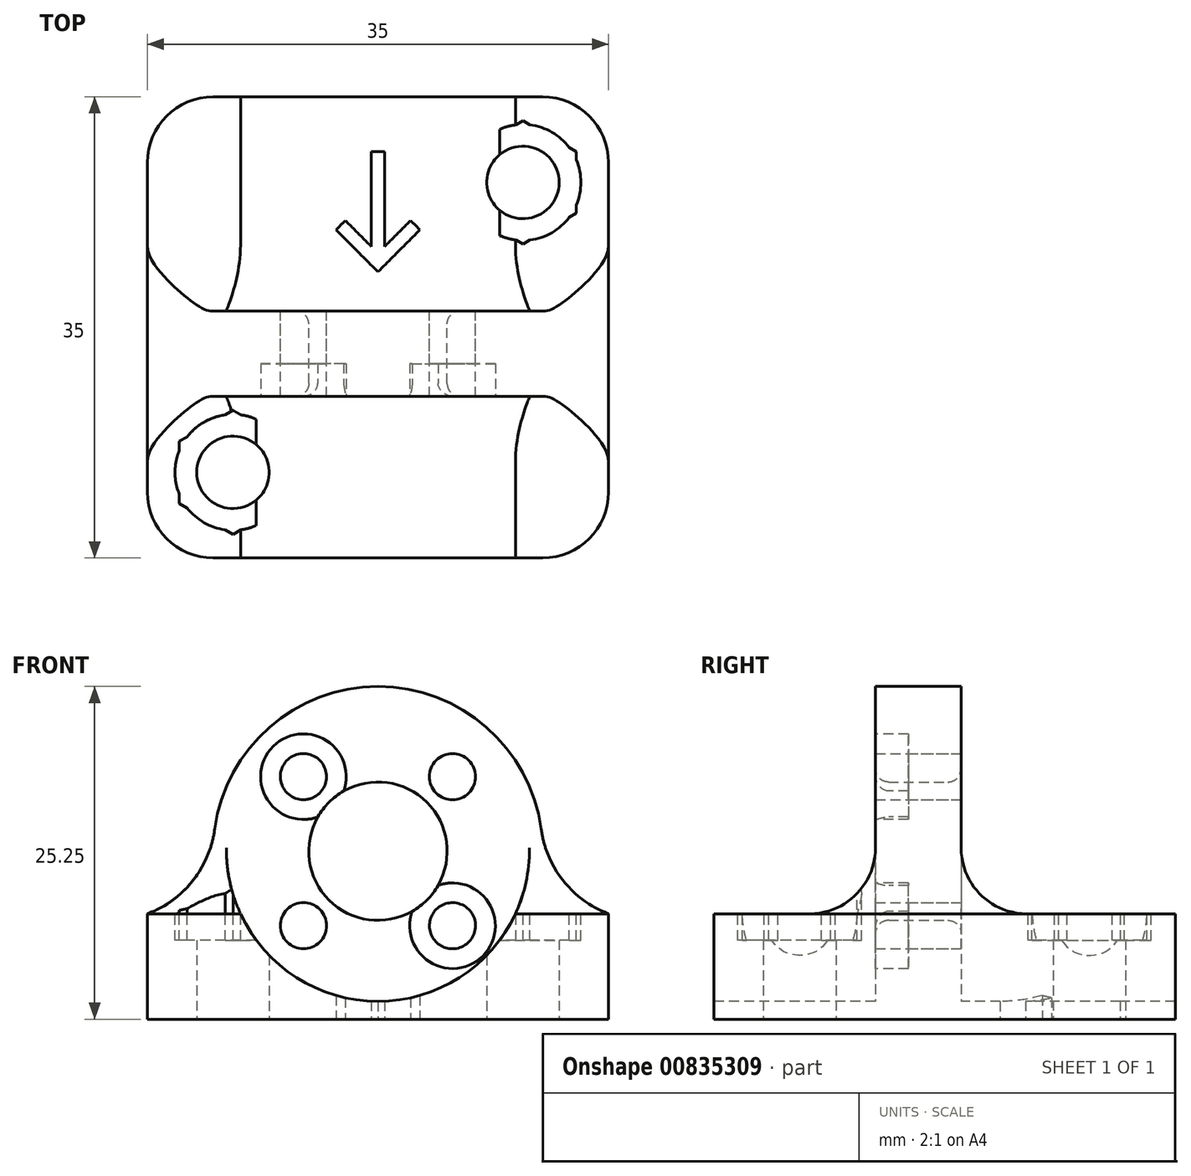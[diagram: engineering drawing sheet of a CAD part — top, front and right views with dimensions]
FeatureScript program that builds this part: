
annotation { "Feature Type Name" : "Feature", "Feature Type Description" : "" }
export const myFeature = defineFeature(function(context is Context, id is Id, definition is map)
    precondition{}
    {
        {
            var Q0;
            Q0=qCreatedBy(makeId("Front.planeOp"),FACE);
            cPlane(context, id + "F0", {"entities" : qUnion([Q0]), "cplaneType" : CPlaneType.OFFSET, "offset" : 2 * mm, "width" : 150 * mm, "height" : 150 * mm});
        }
        {
            var Q0;
            Q0=qCreatedBy(makeId("Top.planeOp"),FACE);
            var sketch = newSketch(context, id + "F1", { "sketchPlane" : qUnion([Q0])});
            skLineSegment(sketch, "E0.bottom", {"start": v(-17.5, 17.5) * mm, "end": v(17.5, 17.5) * mm});
            skLineSegment(sketch, "E0.top", {"start": v(-17.5, -17.5) * mm, "end": v(17.5, -17.5) * mm});
            skLineSegment(sketch, "E0.left", {"start": v(-17.5, 17.5) * mm, "end": v(-17.5, -17.5) * mm});
            skLineSegment(sketch, "E0.right", {"start": v(17.5, 17.5) * mm, "end": v(17.5, -17.5) * mm});
            skPoint(sketch, "E0.middle", {"position": v(0, 0) * mm});
            skLineSegment(sketch, "E1.bottom", {"start": v(-11, 11) * mm, "end": v(11, 11) * mm, "construction": true});
            skLineSegment(sketch, "E1.top", {"start": v(-11, -11) * mm, "end": v(11, -11) * mm, "construction": true});
            skLineSegment(sketch, "E1.left", {"start": v(-11, 11) * mm, "end": v(-11, -11) * mm, "construction": true});
            skLineSegment(sketch, "E1.right", {"start": v(11, 11) * mm, "end": v(11, -11) * mm, "construction": true});
            skCircle(sketch, "E2", {"center": v(-11, 11) * mm, "radius": 2.75 * mm, "construction": true});
            skCircle(sketch, "E3", {"center": v(11, 11) * mm, "radius": 2.75 * mm});
            skCircle(sketch, "E4", {"center": v(11, -11) * mm, "radius": 2.75 * mm, "construction": true});
            skCircle(sketch, "E5", {"center": v(-11, -11) * mm, "radius": 2.75 * mm});
            skSolve(sketch);
        }
        {
            var Q0;
            Q0=qSketchRegion(id+"F1",true);
            extrude(context, id + "F2", {"entities" : qUnion([Q0]), "depth" : 8 * mm, "offsetDistance" : 25 * mm});
        }
        {
            var Q0;
            Q0=qCreatedBy(id+"F0.planeOp",FACE);
            var sketch = newSketch(context, id + "F3", { "sketchPlane" : qUnion([Q0])});
            skLineSegment(sketch, "E6", {"start": v(0, 0) * mm, "end": v(0, 12.75) * mm, "construction": true});
            skArc(sketch, "E7", {"start": v(12.5, 12.75) * mm, "mid": v(0, 25.25) * mm, "end": v(-12.5, 12.75) * mm});
            skLineSegment(sketch, "E8", {"start": v(-12.5, 12.75) * mm, "end": v(-12.5, 0) * mm});
            skLineSegment(sketch, "E9.MirrorCS", {"start": v(12.5, 12.75) * mm, "end": v(12.5, 0) * mm});
            skCircle(sketch, "E10", {"center": v(0, 12.75) * mm, "radius": 5.25 * mm});
            skCircle(sketch, "E11", {"center": v(0, 12.75) * mm, "radius": 8 * mm, "construction": true});
            skLineSegment(sketch, "E12", {"start": v(0, 20.75) * mm, "end": v(0, 4.75) * mm, "construction": true});
            skPoint(sketch, "E12.startSnap0", {"position": v(0, 25.25) * mm});
            skLineSegment(sketch, "E13", {"start": v(-8, 12.75) * mm, "end": v(8, 12.75) * mm, "construction": true});
            skLineSegment(sketch, "E14", {"start": v(0, 12.75) * mm, "end": v(-5.66, 18.4) * mm, "construction": true});
            skLineSegment(sketch, "E15", {"start": v(0, 12.75) * mm, "end": v(-5.66, 7.1) * mm, "construction": true});
            skLineSegment(sketch, "E16.MirrorCS", {"start": v(0, 12.75) * mm, "end": v(5.66, 18.4) * mm, "construction": true});
            skLineSegment(sketch, "E17.MirrorCS", {"start": v(0, 12.75) * mm, "end": v(5.66, 7.1) * mm, "construction": true});
            skCircle(sketch, "E18", {"center": v(-5.66, 18.4) * mm, "radius": 1.75 * mm});
            skCircle(sketch, "E19", {"center": v(-5.66, 7.1) * mm, "radius": 1.75 * mm});
            skCircle(sketch, "E20", {"center": v(5.66, 7.1) * mm, "radius": 1.75 * mm});
            skCircle(sketch, "E21", {"center": v(5.66, 18.4) * mm, "radius": 1.75 * mm});
            skLineSegment(sketch, "E22", {"start": v(-12.5, 0) * mm, "end": v(12.5, 0) * mm});
            skSolve(sketch);
        }
        {
            var Q0;
            Q0=qCreatedBy(makeId("Front.planeOp"),FACE);
            var sketch = newSketch(context, id + "F4", { "sketchPlane" : qUnion([Q0])});
            skLineSegment(sketch, "E23", {"start": v(0, 0) * mm, "end": v(0, 12.85) * mm, "construction": true});
            skCircle(sketch, "E24", {"center": v(0, 12.85) * mm, "radius": 11.5 * mm});
            skSolve(sketch);
        }
        {
            var Q0;
            Q0=qSketchRegion(id+"F4",true);
            extrude(context, id + "F5", {"entities" : qUnion([Q0]), "operationType" : NewBodyOperationType.REMOVE, "endBound" : BoundingType.SYMMETRIC, "oppositeDirection" : true, "depth" : 36 * mm, "offsetDistance" : 25 * mm});
        }
        {
            var Q0;
            Q0=qSketchRegion(id+"F3",true);
            extrude(context, id + "F6", {"entities" : qUnion([Q0]), "operationType" : NewBodyOperationType.ADD, "endBound" : BoundingType.SYMMETRIC, "depth" : 6.5 * mm, "offsetDistance" : 25 * mm});
        }
        {
            var Q0;
            {var subQ0=sQuery(id+"F1.wireOp",EDGE,"E4");var subQ1=sQuery(id+"F1.wireOp",EDGE,"E0.top");var subQ2=sQuery(id+"F1.wireOp",EDGE,"E0.right");var subQ3=sQuery(id+"F1.wireOp",EDGE,"E0.bottom");Q0=makeQuery(id+"F6.boolean.opBoolean","INTERSECT",EDGE,{"derivedFrom":[makeQuery(id+"F5.boolean.opBoolean","SPLIT",FACE,{"disambiguationData":[TD([makeQuery(id+"F2.opExtrude","SWEPT_FACE",FACE,{"disambiguationData":[OSD([subQ2])]})])],"derivedFrom":makeQuery(id+"F2.opExtrude","CAP_FACE",FACE,{"disambiguationData":[OSD([subQ3,subQ1,sQuery(id+"F1.wireOp",EDGE,"E0.left"),subQ2,sQuery(id+"F1.wireOp",EDGE,"E2"),subQ0])],"isStart":false})}),makeQuery(id+"F6.opExtrude","SWEPT_FACE",FACE,{"disambiguationData":[OSD([sQuery(id+"F3.wireOp",EDGE,"E9.MirrorCS")])]})]});}
            var Q1;
            {var subQ0=sQuery(id+"F1.wireOp",EDGE,"E2");var subQ1=sQuery(id+"F1.wireOp",EDGE,"E0.left");var subQ2=sQuery(id+"F1.wireOp",EDGE,"E0.top");var subQ3=sQuery(id+"F1.wireOp",EDGE,"E0.bottom");Q1=makeQuery(id+"F6.boolean.opBoolean","INTERSECT",EDGE,{"derivedFrom":[makeQuery(id+"F5.boolean.opBoolean","SPLIT",FACE,{"disambiguationData":[TD([makeQuery(id+"F2.opExtrude","SWEPT_FACE",FACE,{"disambiguationData":[OSD([subQ1])]})])],"derivedFrom":makeQuery(id+"F2.opExtrude","CAP_FACE",FACE,{"disambiguationData":[OSD([subQ3,subQ2,subQ1,sQuery(id+"F1.wireOp",EDGE,"E0.right"),subQ0,sQuery(id+"F1.wireOp",EDGE,"E4")])],"isStart":false})}),makeQuery(id+"F6.opExtrude","SWEPT_FACE",FACE,{"disambiguationData":[OSD([sQuery(id+"F3.wireOp",EDGE,"E8")])]})]});}
            fillet(context, id + "F7", {"entities" : qUnion([Q0, Q1]), "radius" : 8 * mm, "tangentPropagation" : true, "allowEdgeOverflow" : false});
        }
        {
            var Q0;
            {var subQ0=sQuery(id+"F1.wireOp",EDGE,"E2");var subQ1=sQuery(id+"F1.wireOp",EDGE,"E0.left");var subQ2=sQuery(id+"F1.wireOp",EDGE,"E0.top");var subQ3=sQuery(id+"F1.wireOp",EDGE,"E0.bottom");Q0=makeQuery(id+"F7.opFillet","SPLIT",FACE,{"disambiguationData":[OD(0.0)],"derivedFrom":makeQuery(id+"F5.boolean.opBoolean","SPLIT",FACE,{"disambiguationData":[TD([makeQuery(id+"F2.opExtrude","SWEPT_FACE",FACE,{"disambiguationData":[OSD([subQ1])]})])],"derivedFrom":makeQuery(id+"F2.opExtrude","CAP_FACE",FACE,{"disambiguationData":[OSD([subQ3,subQ2,subQ1,sQuery(id+"F1.wireOp",EDGE,"E0.right"),subQ0,sQuery(id+"F1.wireOp",EDGE,"E4")])],"isStart":false})})});}
            var sketch = newSketch(context, id + "F8", { "sketchPlane" : qUnion([Q0])});
            skPoint(sketch, "E25.0.midPoint.positionSnap0", {"position": v(5.2, -11) * mm});
            skLineSegment(sketch, "E26", {"start": v(17.5, 17.5) * mm, "end": v(-17.5, -17.5) * mm, "construction": true});
            skCircle(sketch, "E27.cCircle", {"center": v(11, 11) * mm, "radius": 4.05 * mm, "construction": true});
            skLineSegment(sketch, "E27.0", {"start": v(15.05, 13.34) * mm, "end": v(15.05, 8.66) * mm});
            skLineSegment(sketch, "E27.1", {"start": v(15.05, 8.66) * mm, "end": v(11, 6.32) * mm});
            skLineSegment(sketch, "E27.2", {"start": v(11, 6.32) * mm, "end": v(6.95, 8.66) * mm});
            skLineSegment(sketch, "E27.3", {"start": v(6.95, 8.66) * mm, "end": v(6.95, 13.34) * mm});
            skLineSegment(sketch, "E27.4", {"start": v(6.95, 13.34) * mm, "end": v(11, 15.68) * mm});
            skLineSegment(sketch, "E27.5", {"start": v(11, 15.68) * mm, "end": v(15.05, 13.34) * mm});
            skPoint(sketch, "E27.0.midPoint", {"position": v(15.05, 11) * mm});
            skCircle(sketch, "E28.cCircle", {"center": v(-11, -11) * mm, "radius": 4.08 * mm, "construction": true});
            skLineSegment(sketch, "E28.0", {"start": v(-11, -6.3) * mm, "end": v(-6.93, -8.65) * mm});
            skLineSegment(sketch, "E28.1", {"start": v(-6.93, -8.65) * mm, "end": v(-6.93, -13.35) * mm});
            skLineSegment(sketch, "E28.2", {"start": v(-6.93, -13.35) * mm, "end": v(-11, -15.7) * mm});
            skLineSegment(sketch, "E28.3", {"start": v(-11, -15.7) * mm, "end": v(-15.08, -13.35) * mm});
            skLineSegment(sketch, "E28.4", {"start": v(-15.07, -13.35) * mm, "end": v(-15.07, -8.65) * mm});
            skLineSegment(sketch, "E28.5", {"start": v(-15.07, -8.65) * mm, "end": v(-11, -6.3) * mm});
            skPoint(sketch, "E28.0.midPoint", {"position": v(-8.96, -7.47) * mm});
            skSolve(sketch);
        }
        {
            var Q0;
            Q0=qSketchRegion(id+"F8",true);
            extrude(context, id + "F9", {"entities" : qUnion([Q0]), "operationType" : NewBodyOperationType.REMOVE, "oppositeDirection" : true, "depth" : 2 * mm, "offsetDistance" : 25 * mm});
        }
        {
            var Q0;
            {var subQ0=sQuery(id+"F1.wireOp",EDGE,"E2");var subQ1=sQuery(id+"F1.wireOp",EDGE,"E0.left");var subQ2=sQuery(id+"F1.wireOp",EDGE,"E0.top");var subQ3=sQuery(id+"F1.wireOp",EDGE,"E0.bottom");Q0=makeQuery(id+"F7.opFillet","SPLIT",FACE,{"disambiguationData":[OD(0.0)],"derivedFrom":makeQuery(id+"F5.boolean.opBoolean","SPLIT",FACE,{"disambiguationData":[TD([makeQuery(id+"F2.opExtrude","SWEPT_FACE",FACE,{"disambiguationData":[OSD([subQ1])]})])],"derivedFrom":makeQuery(id+"F2.opExtrude","CAP_FACE",FACE,{"disambiguationData":[OSD([subQ3,subQ2,subQ1,sQuery(id+"F1.wireOp",EDGE,"E0.right"),subQ0,sQuery(id+"F1.wireOp",EDGE,"E4")])],"isStart":false})})});}
            var sketch = newSketch(context, id + "F10", { "sketchPlane" : qUnion([Q0])});
            skCircle(sketch, "E29", {"center": v(11, 11) * mm, "radius": 4.4 * mm});
            skCircle(sketch, "E30", {"center": v(-11, -11) * mm, "radius": 4.4 * mm});
            skSolve(sketch);
        }
        {
            var Q0;
            Q0=qSketchRegion(id+"F10",true);
            extrude(context, id + "F11", {"entities" : qUnion([Q0]), "operationType" : NewBodyOperationType.REMOVE, "oppositeDirection" : true, "depth" : 2 * mm, "offsetDistance" : 25 * mm});
        }
        {
            var Q0;
            {var subQ0=sQuery(id+"F1.wireOp",EDGE,"E4");var subQ1=sQuery(id+"F1.wireOp",EDGE,"E0.top");var subQ2=sQuery(id+"F1.wireOp",EDGE,"E0.right");var subQ3=sQuery(id+"F1.wireOp",EDGE,"E0.bottom");Q0=makeQuery(id+"F6.boolean.opBoolean","INTERSECT",EDGE,{"derivedFrom":[makeQuery(id+"F5.boolean.opBoolean","SPLIT",FACE,{"disambiguationData":[TD([makeQuery(id+"F2.opExtrude","SWEPT_FACE",FACE,{"disambiguationData":[OSD([subQ2])]})])],"derivedFrom":makeQuery(id+"F2.opExtrude","CAP_FACE",FACE,{"disambiguationData":[OSD([subQ3,subQ1,sQuery(id+"F1.wireOp",EDGE,"E0.left"),subQ2,sQuery(id+"F1.wireOp",EDGE,"E2"),subQ0])],"isStart":false})}),makeQuery(id+"F6.opExtrude","CAP_FACE",FACE,{"disambiguationData":[OSD([sQuery(id+"F3.wireOp",EDGE,"E7"),sQuery(id+"F3.wireOp",EDGE,"E8"),sQuery(id+"F3.wireOp",EDGE,"E9.MirrorCS"),sQuery(id+"F3.wireOp",EDGE,"E10"),sQuery(id+"F3.wireOp",EDGE,"E18"),sQuery(id+"F3.wireOp",EDGE,"E19"),sQuery(id+"F3.wireOp",EDGE,"E20"),sQuery(id+"F3.wireOp",EDGE,"E21"),sQuery(id+"F3.wireOp",EDGE,"E22")])],"isStart":true})]});}
            var Q1;
            {var subQ0=sQuery(id+"F1.wireOp",EDGE,"E2");var subQ1=sQuery(id+"F1.wireOp",EDGE,"E0.left");var subQ2=sQuery(id+"F1.wireOp",EDGE,"E0.top");var subQ3=sQuery(id+"F1.wireOp",EDGE,"E0.bottom");Q1=makeQuery(id+"F6.boolean.opBoolean","INTERSECT",EDGE,{"derivedFrom":[makeQuery(id+"F5.boolean.opBoolean","SPLIT",FACE,{"disambiguationData":[TD([makeQuery(id+"F2.opExtrude","SWEPT_FACE",FACE,{"disambiguationData":[OSD([subQ1])]})])],"derivedFrom":makeQuery(id+"F2.opExtrude","CAP_FACE",FACE,{"disambiguationData":[OSD([subQ3,subQ2,subQ1,sQuery(id+"F1.wireOp",EDGE,"E0.right"),subQ0,sQuery(id+"F1.wireOp",EDGE,"E4")])],"isStart":false})}),makeQuery(id+"F6.opExtrude","CAP_FACE",FACE,{"disambiguationData":[OSD([sQuery(id+"F3.wireOp",EDGE,"E7"),sQuery(id+"F3.wireOp",EDGE,"E8"),sQuery(id+"F3.wireOp",EDGE,"E9.MirrorCS"),sQuery(id+"F3.wireOp",EDGE,"E10"),sQuery(id+"F3.wireOp",EDGE,"E18"),sQuery(id+"F3.wireOp",EDGE,"E19"),sQuery(id+"F3.wireOp",EDGE,"E20"),sQuery(id+"F3.wireOp",EDGE,"E21"),sQuery(id+"F3.wireOp",EDGE,"E22")])],"isStart":true})]});}
            var Q2;
            {var subQ0=sQuery(id+"F1.wireOp",EDGE,"E2");var subQ1=sQuery(id+"F1.wireOp",EDGE,"E0.left");var subQ2=sQuery(id+"F1.wireOp",EDGE,"E0.top");var subQ3=sQuery(id+"F1.wireOp",EDGE,"E0.bottom");Q2=makeQuery(id+"F6.boolean.opBoolean","INTERSECT",EDGE,{"derivedFrom":[makeQuery(id+"F5.boolean.opBoolean","SPLIT",FACE,{"disambiguationData":[TD([makeQuery(id+"F2.opExtrude","SWEPT_FACE",FACE,{"disambiguationData":[OSD([subQ1])]})])],"derivedFrom":makeQuery(id+"F2.opExtrude","CAP_FACE",FACE,{"disambiguationData":[OSD([subQ3,subQ2,subQ1,sQuery(id+"F1.wireOp",EDGE,"E0.right"),subQ0,sQuery(id+"F1.wireOp",EDGE,"E4")])],"isStart":false})}),makeQuery(id+"F6.opExtrude","CAP_FACE",FACE,{"disambiguationData":[OSD([sQuery(id+"F3.wireOp",EDGE,"E7"),sQuery(id+"F3.wireOp",EDGE,"E8"),sQuery(id+"F3.wireOp",EDGE,"E9.MirrorCS"),sQuery(id+"F3.wireOp",EDGE,"E10"),sQuery(id+"F3.wireOp",EDGE,"E18"),sQuery(id+"F3.wireOp",EDGE,"E19"),sQuery(id+"F3.wireOp",EDGE,"E20"),sQuery(id+"F3.wireOp",EDGE,"E21"),sQuery(id+"F3.wireOp",EDGE,"E22")])],"isStart":false})]});}
            var Q3;
            {var subQ0=sQuery(id+"F1.wireOp",EDGE,"E4");var subQ1=sQuery(id+"F1.wireOp",EDGE,"E0.top");var subQ2=sQuery(id+"F1.wireOp",EDGE,"E0.right");var subQ3=sQuery(id+"F1.wireOp",EDGE,"E0.bottom");Q3=makeQuery(id+"F6.boolean.opBoolean","INTERSECT",EDGE,{"derivedFrom":[makeQuery(id+"F5.boolean.opBoolean","SPLIT",FACE,{"disambiguationData":[TD([makeQuery(id+"F2.opExtrude","SWEPT_FACE",FACE,{"disambiguationData":[OSD([subQ2])]})])],"derivedFrom":makeQuery(id+"F2.opExtrude","CAP_FACE",FACE,{"disambiguationData":[OSD([subQ3,subQ1,sQuery(id+"F1.wireOp",EDGE,"E0.left"),subQ2,sQuery(id+"F1.wireOp",EDGE,"E2"),subQ0])],"isStart":false})}),makeQuery(id+"F6.opExtrude","CAP_FACE",FACE,{"disambiguationData":[OSD([sQuery(id+"F3.wireOp",EDGE,"E7"),sQuery(id+"F3.wireOp",EDGE,"E8"),sQuery(id+"F3.wireOp",EDGE,"E9.MirrorCS"),sQuery(id+"F3.wireOp",EDGE,"E10"),sQuery(id+"F3.wireOp",EDGE,"E18"),sQuery(id+"F3.wireOp",EDGE,"E19"),sQuery(id+"F3.wireOp",EDGE,"E20"),sQuery(id+"F3.wireOp",EDGE,"E21"),sQuery(id+"F3.wireOp",EDGE,"E22")])],"isStart":false})]});}
            var Q4;
            Q4=makeQuery(id+"F2.opExtrude","SWEPT_EDGE",EDGE,{"disambiguationData":[OSD([sQuery(id+"F1.wireOp",EDGE,"E0.top"),sQuery(id+"F1.wireOp",EDGE,"E0.left")])]});
            var Q5;
            Q5=makeQuery(id+"F2.opExtrude","SWEPT_EDGE",EDGE,{"disambiguationData":[OSD([sQuery(id+"F1.wireOp",EDGE,"E0.bottom"),sQuery(id+"F1.wireOp",EDGE,"E0.left")])]});
            var Q6;
            Q6=makeQuery(id+"F2.opExtrude","SWEPT_EDGE",EDGE,{"disambiguationData":[OSD([sQuery(id+"F1.wireOp",EDGE,"E0.bottom"),sQuery(id+"F1.wireOp",EDGE,"E0.right")])]});
            var Q7;
            Q7=makeQuery(id+"F2.opExtrude","SWEPT_EDGE",EDGE,{"disambiguationData":[OSD([sQuery(id+"F1.wireOp",EDGE,"E0.top"),sQuery(id+"F1.wireOp",EDGE,"E0.right")])]});
            fillet(context, id + "F12", {"entities" : qUnion([Q0, Q1, Q2, Q3, Q4, Q5, Q6, Q7]), "radius" : 5 * mm, "tangentPropagation" : true, "allowEdgeOverflow" : false});
        }
        {
            var Q0;
            Q0=makeQuery(id+"F6.opExtrude","CAP_FACE",FACE,{"disambiguationData":[OSD([sQuery(id+"F3.wireOp",EDGE,"E7"),sQuery(id+"F3.wireOp",EDGE,"E8"),sQuery(id+"F3.wireOp",EDGE,"E9.MirrorCS"),sQuery(id+"F3.wireOp",EDGE,"E10"),sQuery(id+"F3.wireOp",EDGE,"E18"),sQuery(id+"F3.wireOp",EDGE,"E20"),sQuery(id+"F3.wireOp",EDGE,"E22")])],"isStart":false});
            var sketch = newSketch(context, id + "F13", { "sketchPlane" : qUnion([Q0])});
            skCircle(sketch, "E31", {"center": v(-5.66, 18.4) * mm, "radius": 3.25 * mm});
            skCircle(sketch, "E32", {"center": v(5.66, 7.1) * mm, "radius": 3.25 * mm});
            skLineSegment(sketch, "E33", {"start": v(0, 12.75) * mm, "end": v(12.71, 12.75) * mm, "construction": true});
            skCircle(sketch, "E34.MirrorC", {"center": v(5.66, 18.4) * mm, "radius": 3.25 * mm});
            skCircle(sketch, "E35.MirrorC", {"center": v(-5.66, 7.1) * mm, "radius": 3.25 * mm});
            skSolve(sketch);
        }
        {
            var Q0;
            Q0=makeQuery(id+"F13.imprint","IMPRINT",FACE,{"disambiguationData":[TD([[makeQuery(id+"F13.imprint","IMPRINT",EDGE,{"derivedFrom":sQuery(id+"F13.wireOp",EDGE,"E31")}),1.0]])]});
            var Q1;
            Q1=makeQuery(id+"F13.imprint","IMPRINT",FACE,{"disambiguationData":[TD([[makeQuery(id+"F13.imprint","IMPRINT",EDGE,{"derivedFrom":sQuery(id+"F13.wireOp",EDGE,"E32")}),1.0]])]});
            var Q2;
            Q2=makeQuery(id+"F13.imprint","IMPRINT",FACE,{"disambiguationData":[TD([[makeQuery(id+"F13.imprint","IMPRINT",EDGE,{"derivedFrom":makeQuery(id+"F6.opExtrude","CAP_EDGE",EDGE,{"disambiguationData":[OSD([sQuery(id+"F3.wireOp",EDGE,"E18")])],"isStart":false})}),-1.0]])]});
            var Q3;
            Q3=makeQuery(id+"F13.imprint","IMPRINT",FACE,{"disambiguationData":[TD([[makeQuery(id+"F13.imprint","IMPRINT",EDGE,{"derivedFrom":makeQuery(id+"F6.opExtrude","CAP_EDGE",EDGE,{"disambiguationData":[OSD([sQuery(id+"F3.wireOp",EDGE,"E20")])],"isStart":false})}),-1.0]])]});
            var Q4;
            {var subQ0=sQuery(id+"F13.wireOp",EDGE,"E34.MirrorC");var subQ1=makeQuery(id+"F6.opExtrude","CAP_EDGE",EDGE,{"disambiguationData":[OSD([sQuery(id+"F3.wireOp",EDGE,"E10")])],"isStart":false});var subQ2=makeQuery(id+"F13.imprint","INTERSECT",VERTEX,{"disambiguationData":[OD(0.0)],"derivedFrom":[subQ1,subQ0]});Q4=makeQuery(id+"F13.imprint","IMPRINT",FACE,{"disambiguationData":[TD([[makeQuery(id+"F13.imprint","IMPRINT",EDGE,{"disambiguationData":[TD([[subQ2,-1.0]])],"derivedFrom":subQ0}),-1.0]])]});}
            var Q5;
            {var subQ0=sQuery(id+"F13.wireOp",EDGE,"E35.MirrorC");var subQ1=makeQuery(id+"F6.opExtrude","CAP_EDGE",EDGE,{"disambiguationData":[OSD([sQuery(id+"F3.wireOp",EDGE,"E10")])],"isStart":false});var subQ2=makeQuery(id+"F13.imprint","INTERSECT",VERTEX,{"disambiguationData":[OD(0.0)],"derivedFrom":[subQ1,subQ0]});Q5=makeQuery(id+"F13.imprint","IMPRINT",FACE,{"disambiguationData":[TD([[makeQuery(id+"F13.imprint","IMPRINT",EDGE,{"disambiguationData":[TD([[subQ2,1.0]])],"derivedFrom":subQ0}),-1.0]])]});}
            var Q6;
            Q6=makeQuery(id+"F6.opExtrude","CAP_FACE",FACE,{"disambiguationData":[OSD([sQuery(id+"F3.wireOp",EDGE,"E7"),sQuery(id+"F3.wireOp",EDGE,"E8"),sQuery(id+"F3.wireOp",EDGE,"E9.MirrorCS"),sQuery(id+"F3.wireOp",EDGE,"E10"),sQuery(id+"F3.wireOp",EDGE,"E18"),sQuery(id+"F3.wireOp",EDGE,"E20"),sQuery(id+"F3.wireOp",EDGE,"E22")])],"isStart":true});
            extrude(context, id + "F14", {"entities" : qUnion([Q0, Q1, Q2, Q3, Q4, Q5]), "operationType" : NewBodyOperationType.REMOVE, "oppositeDirection" : true, "depth" : 2.5 * mm, "endBoundEntityFace" : qUnion([Q6]), "hasOffset" : true, "offsetDistance" : 5 * mm, "offsetOppositeDirection" : true});
        }
        {
            var Q0;
            Q0=makeQuery(id+"F2.opExtrude","CAP_FACE",FACE,{"disambiguationData":[OSD([sQuery(id+"F1.wireOp",EDGE,"E0.bottom"),sQuery(id+"F1.wireOp",EDGE,"E0.top"),sQuery(id+"F1.wireOp",EDGE,"E0.left"),sQuery(id+"F1.wireOp",EDGE,"E0.right"),sQuery(id+"F1.wireOp",EDGE,"E3"),sQuery(id+"F1.wireOp",EDGE,"E5")])],"isStart":true});
            var sketch = newSketch(context, id + "F15", { "sketchPlane" : qUnion([Q0])});
            skLineSegment(sketch, "E36", {"start": v(0, 0) * mm, "end": v(0, -17.5) * mm, "construction": true});
            skLineSegment(sketch, "E37", {"start": v(0, -4.22) * mm, "end": v(-3.18, -7.4) * mm});
            skLineSegment(sketch, "E38", {"start": v(-3.18, -7.4) * mm, "end": v(-2.47, -8.1) * mm});
            skLineSegment(sketch, "E39", {"start": v(-2.47, -8.1) * mm, "end": v(-0.5, -6.13) * mm});
            skLineSegment(sketch, "E40", {"start": v(-0.5, -6.13) * mm, "end": v(-0.5, -13.33) * mm});
            skLineSegment(sketch, "E41", {"start": v(-0.5, -13.33) * mm, "end": v(0, -13.33) * mm});
            skLineSegment(sketch, "E42.MirrorCS", {"start": v(0.5, -13.33) * mm, "end": v(0, -13.33) * mm});
            skLineSegment(sketch, "E43.MirrorCS", {"start": v(3.18, -7.4) * mm, "end": v(2.47, -8.1) * mm});
            skLineSegment(sketch, "E44.MirrorCS", {"start": v(0.5, -6.13) * mm, "end": v(0.5, -13.33) * mm});
            skLineSegment(sketch, "E45.MirrorCS", {"start": v(2.47, -8.1) * mm, "end": v(0.5, -6.13) * mm});
            skLineSegment(sketch, "E46.MirrorCS", {"start": v(0, -4.22) * mm, "end": v(3.18, -7.4) * mm});
            skSolve(sketch);
        }
        {
            var Q0;
            Q0=qSketchRegion(id+"F15",true);
            extrude(context, id + "F16", {"entities" : qUnion([Q0]), "operationType" : NewBodyOperationType.REMOVE, "oppositeDirection" : true, "depth" : 3 * mm, "offsetDistance" : 25 * mm});
        }
        {
            var Q0;
            Q0=makeQuery(id+"F14.boolean.opBoolean","COPY",EDGE,{"derivedFrom":makeQuery(id+"F14.opExtrude","CAP_EDGE",EDGE,{"disambiguationData":[OSD([sQuery(id+"F13.wireOp",EDGE,"E31")])],"isStart":true})});
            var Q1;
            Q1=makeQuery(id+"F14.boolean.opBoolean","COPY",EDGE,{"derivedFrom":makeQuery(id+"F14.opExtrude","CAP_EDGE",EDGE,{"disambiguationData":[OSD([sQuery(id+"F13.wireOp",EDGE,"E34.MirrorC")])],"isStart":true})});
            var Q2;
            Q2=makeQuery(id+"F14.boolean.opBoolean","COPY",EDGE,{"derivedFrom":makeQuery(id+"F14.opExtrude","CAP_EDGE",EDGE,{"disambiguationData":[OSD([sQuery(id+"F13.wireOp",EDGE,"E32")])],"isStart":true})});
            var Q3;
            Q3=makeQuery(id+"F14.boolean.opBoolean","COPY",EDGE,{"derivedFrom":makeQuery(id+"F14.opExtrude","CAP_EDGE",EDGE,{"disambiguationData":[OSD([sQuery(id+"F13.wireOp",EDGE,"E35.MirrorC")])],"isStart":true})});
            var Q4;
            {var subQ0=sQuery(id+"F3.wireOp",EDGE,"E10");Q4=makeQuery(id+"F14.boolean.opBoolean","SPLIT",EDGE,{"disambiguationData":[TD([makeQuery(id+"F6.opExtrude","CAP_FACE",FACE,{"disambiguationData":[OSD([sQuery(id+"F3.wireOp",EDGE,"E7"),sQuery(id+"F3.wireOp",EDGE,"E8"),sQuery(id+"F3.wireOp",EDGE,"E9.MirrorCS"),subQ0,sQuery(id+"F3.wireOp",EDGE,"E18"),sQuery(id+"F3.wireOp",EDGE,"E19"),sQuery(id+"F3.wireOp",EDGE,"E20"),sQuery(id+"F3.wireOp",EDGE,"E21"),sQuery(id+"F3.wireOp",EDGE,"E22")])],"isStart":false}),makeQuery(id+"F6.opExtrude","SWEPT_FACE",FACE,{"disambiguationData":[OSD([subQ0])]}),makeQuery(id+"F14.opExtrude","SWEPT_FACE",FACE,{"disambiguationData":[OSD([sQuery(id+"F13.wireOp",EDGE,"E31")])]}),makeQuery(id+"F14.opExtrude","SWEPT_FACE",FACE,{"disambiguationData":[OSD([sQuery(id+"F13.wireOp",EDGE,"E35.MirrorC")])]})])],"derivedFrom":makeQuery(id+"F6.opExtrude","CAP_EDGE",EDGE,{"disambiguationData":[OSD([subQ0])],"isStart":false})});}
            var Q5;
            {var subQ0=sQuery(id+"F3.wireOp",EDGE,"E10");Q5=makeQuery(id+"F14.boolean.opBoolean","SPLIT",EDGE,{"disambiguationData":[TD([makeQuery(id+"F6.opExtrude","CAP_FACE",FACE,{"disambiguationData":[OSD([sQuery(id+"F3.wireOp",EDGE,"E7"),sQuery(id+"F3.wireOp",EDGE,"E8"),sQuery(id+"F3.wireOp",EDGE,"E9.MirrorCS"),subQ0,sQuery(id+"F3.wireOp",EDGE,"E18"),sQuery(id+"F3.wireOp",EDGE,"E19"),sQuery(id+"F3.wireOp",EDGE,"E20"),sQuery(id+"F3.wireOp",EDGE,"E21"),sQuery(id+"F3.wireOp",EDGE,"E22")])],"isStart":false}),makeQuery(id+"F6.opExtrude","SWEPT_FACE",FACE,{"disambiguationData":[OSD([subQ0])]}),makeQuery(id+"F14.opExtrude","SWEPT_FACE",FACE,{"disambiguationData":[OSD([sQuery(id+"F13.wireOp",EDGE,"E31")])]}),makeQuery(id+"F14.opExtrude","SWEPT_FACE",FACE,{"disambiguationData":[OSD([sQuery(id+"F13.wireOp",EDGE,"E34.MirrorC")])]})])],"derivedFrom":makeQuery(id+"F6.opExtrude","CAP_EDGE",EDGE,{"disambiguationData":[OSD([subQ0])],"isStart":false})});}
            var Q6;
            {var subQ0=sQuery(id+"F3.wireOp",EDGE,"E10");Q6=makeQuery(id+"F14.boolean.opBoolean","SPLIT",EDGE,{"disambiguationData":[TD([makeQuery(id+"F6.opExtrude","CAP_FACE",FACE,{"disambiguationData":[OSD([sQuery(id+"F3.wireOp",EDGE,"E7"),sQuery(id+"F3.wireOp",EDGE,"E8"),sQuery(id+"F3.wireOp",EDGE,"E9.MirrorCS"),subQ0,sQuery(id+"F3.wireOp",EDGE,"E18"),sQuery(id+"F3.wireOp",EDGE,"E19"),sQuery(id+"F3.wireOp",EDGE,"E20"),sQuery(id+"F3.wireOp",EDGE,"E21"),sQuery(id+"F3.wireOp",EDGE,"E22")])],"isStart":false}),makeQuery(id+"F6.opExtrude","SWEPT_FACE",FACE,{"disambiguationData":[OSD([subQ0])]}),makeQuery(id+"F14.opExtrude","SWEPT_FACE",FACE,{"disambiguationData":[OSD([sQuery(id+"F13.wireOp",EDGE,"E32")])]}),makeQuery(id+"F14.opExtrude","SWEPT_FACE",FACE,{"disambiguationData":[OSD([sQuery(id+"F13.wireOp",EDGE,"E34.MirrorC")])]})])],"derivedFrom":makeQuery(id+"F6.opExtrude","CAP_EDGE",EDGE,{"disambiguationData":[OSD([subQ0])],"isStart":false})});}
            var Q7;
            {var subQ0=sQuery(id+"F3.wireOp",EDGE,"E10");Q7=makeQuery(id+"F14.boolean.opBoolean","SPLIT",EDGE,{"disambiguationData":[TD([makeQuery(id+"F6.opExtrude","CAP_FACE",FACE,{"disambiguationData":[OSD([sQuery(id+"F3.wireOp",EDGE,"E7"),sQuery(id+"F3.wireOp",EDGE,"E8"),sQuery(id+"F3.wireOp",EDGE,"E9.MirrorCS"),subQ0,sQuery(id+"F3.wireOp",EDGE,"E18"),sQuery(id+"F3.wireOp",EDGE,"E19"),sQuery(id+"F3.wireOp",EDGE,"E20"),sQuery(id+"F3.wireOp",EDGE,"E21"),sQuery(id+"F3.wireOp",EDGE,"E22")])],"isStart":false}),makeQuery(id+"F6.opExtrude","SWEPT_FACE",FACE,{"disambiguationData":[OSD([subQ0])]}),makeQuery(id+"F14.opExtrude","SWEPT_FACE",FACE,{"disambiguationData":[OSD([sQuery(id+"F13.wireOp",EDGE,"E32")])]}),makeQuery(id+"F14.opExtrude","SWEPT_FACE",FACE,{"disambiguationData":[OSD([sQuery(id+"F13.wireOp",EDGE,"E35.MirrorC")])]})])],"derivedFrom":makeQuery(id+"F6.opExtrude","CAP_EDGE",EDGE,{"disambiguationData":[OSD([subQ0])],"isStart":false})});}
            var Q8;
            Q8=makeQuery(id+"F6.opExtrude","CAP_EDGE",EDGE,{"disambiguationData":[OSD([sQuery(id+"F3.wireOp",EDGE,"E10")])],"isStart":true});
            fillet(context, id + "F17", {"entities" : qUnion([Q0, Q1, Q2, Q3, Q4, Q5, Q6, Q7, Q8]), "radius" : 1 * mm, "tangentPropagation" : true, "allowEdgeOverflow" : false});
        }
    });
